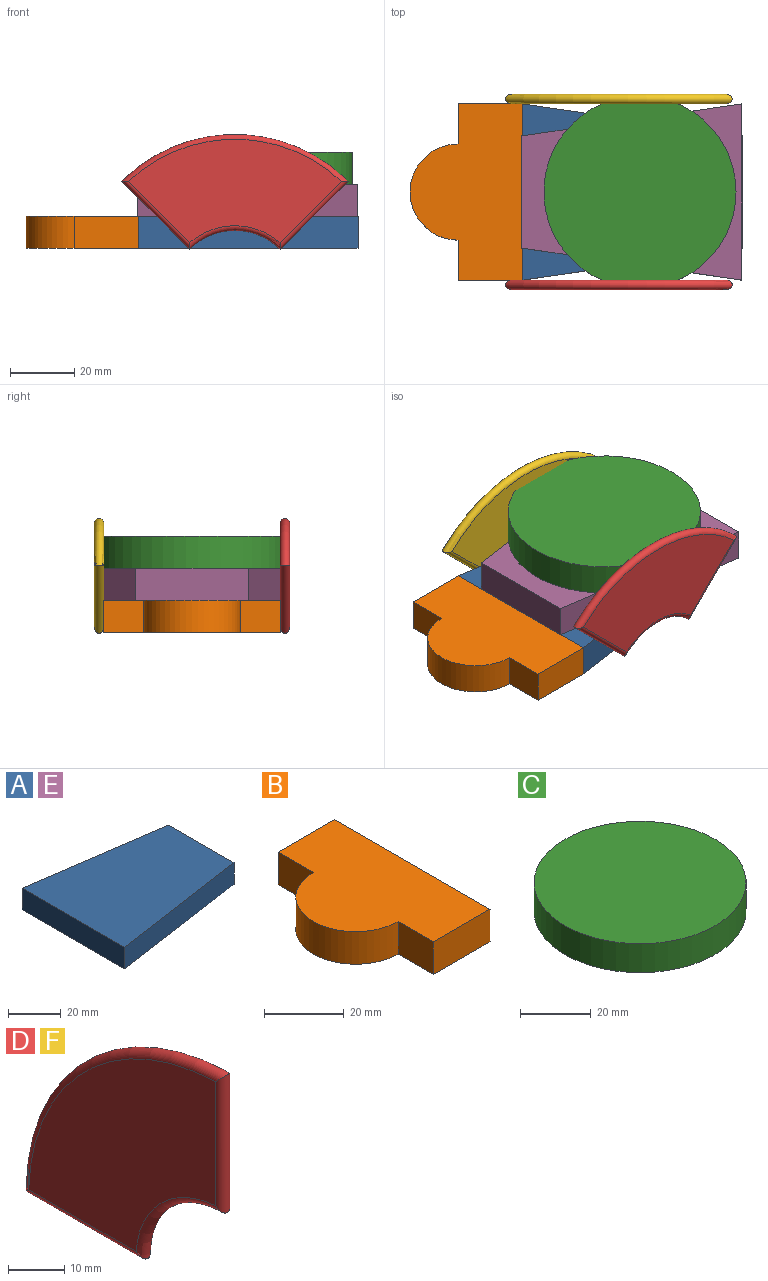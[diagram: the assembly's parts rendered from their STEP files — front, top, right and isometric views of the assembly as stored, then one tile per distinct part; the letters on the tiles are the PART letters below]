
ASSEMBLY  parts=6 mates=6
PART A: 6 faces, bbox 68.6x55x10 mm
  f0: plane 35x10mm, normal (1,0,0), area 350mm2, adj f1,f2,f3,f4
  f1: plane 68.63x55mm, normal (0,0,-1), area 3088.3mm2, adj f0,f3,f4,f5
  f2: plane 68.63x55mm, normal (0,0,1), area 3088.3mm2, adj f0,f3,f4,f5
  f3: plane 68.63x10mm, normal (0.14,0.99,0), area 693.5mm2, adj f0,f1,f2,f5
  f4: plane 68.63x10mm, normal (0.14,-0.99,0), area 693.5mm2, adj f0,f1,f2,f5
  f5: plane 55x10mm, normal (-1,0,0), area 550mm2, adj f1,f2,f3,f4
PART B: 10 faces, bbox 35x55x10 mm
  f0: plane 10x0mm, normal (0.14,-0.99,0), area 0mm2, adj f8,f9
  f1: plane 10x0mm, normal (0.14,0.99,0), area 0mm2, adj f4,f9
  f2: plane 55x35mm, normal (0,0,1), area 1453.4mm2, adj f4,f5,f6,f7,f8,f9
  f3: plane 55x35mm, normal (0,0,-1), area 1453.4mm2, adj f4,f5,f6,f7,f8,f9
  f4: plane 20x10mm, normal (0,1,0), area 200mm2, adj f1,f2,f3,f5
  f5: plane 12.5x10mm, normal (-1,0,0), area 125mm2, adj f2,f3,f4,f6
  f6: cylinder r=15mm len=30mm, axis (0,0,-1), area 471.2mm2, adj f2,f3,f5,f7
  f7: plane 12.5x10mm, normal (-1,0,0), area 125mm2, adj f2,f3,f6,f8
  f8: plane 20x10mm, normal (0,-1,0), area 200mm2, adj f0,f2,f3,f7
  f9: plane 55x10mm, normal (1,0,0), area 550mm2, adj f0,f1,f2,f3
PART C: 3 faces, bbox 60x60x10 mm
  f0: cylinder r=30mm len=60mm, axis (0,0,-1), area 1885mm2, adj f1,f2
  f1: plane 60x60mm, normal (0,0,1), area 2827.4mm2, adj f0
  f2: plane 60x60mm, normal (0,0,-1), area 2827.4mm2, adj f0
PART D: 6 faces, bbox 3x54.1x54.1 mm
  f0: plane 46.98x46.98mm, normal (1,0,0), area 1403.4mm2, adj f2,f3,f4,f5
  f1: plane 46.98x46.98mm, normal (-1,0,0), area 1403.4mm2, adj f2,f3,f4,f5
  f2: cylinder r=1.5mm len=30mm, axis (0,0,1), area 136.3mm2, adj f0,f1,f3,f4
  f3: torus R=21.5mm, axis (1,0,0), area 146.9mm2, adj f0,f1,f2,f5
  f4: torus R=48.5mm, axis (1,0,0), area 360.9mm2, adj f0,f1,f2,f5
  f5: cylinder r=1.5mm len=30mm, axis (0,-1,0), area 136.3mm2, adj f0,f1,f3,f4
PART E: same geometry as A
PART F: same geometry as D
PLACE A t=(0,0,-0.82)mm
PLACE B t=(0,0,-0.82)mm
PLACE C t=(26.66,33.22,19.18)mm
PLACE D rot(axis=(0.36,-0.36,-0.86),98.4deg) t=(61.71,12.53,45.99)mm
PLACE E rot(axis=(0,0,1),180deg) t=(63.51,80.06,9.18)mm
PLACE F rot(axis=(0.36,0.36,0.86),98.4deg) t=(-6.36,67.53,45.99)mm
MATE fastened B.f9 <-> A.f5  axis (1,0,0) through (-2.52,40.03,4.18)mm
MATE fastened C.f0 <-> E.f2  axis (0,0,-1) through (34.25,40.03,19.18)mm
MATE planar F.f1 <-> B.f4  axis (0,-1,0) through (27.67,67.53,18.26)mm
MATE planar E.f1 <-> A.f2  axis (0,0,-1) through (34.25,40.03,9.18)mm
MATE planar D.f1 <-> B.f8  axis (0,1,0) through (27.68,12.53,18.26)mm
MATE planar E.f1 <-> A.f2  axis (0,0,-1) through (34.25,40.03,9.18)mm
